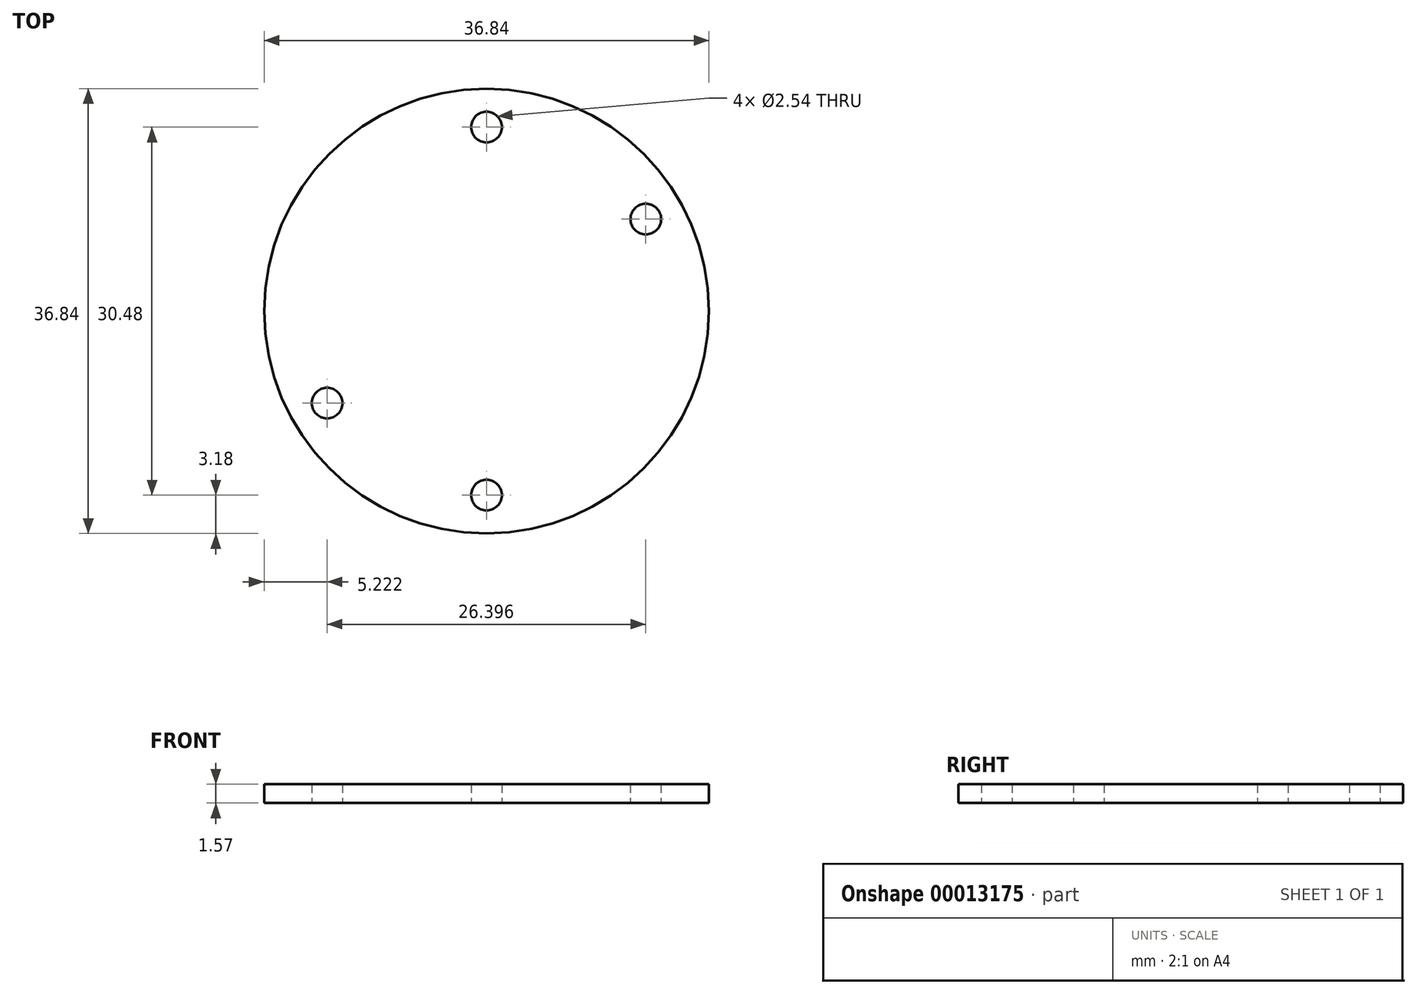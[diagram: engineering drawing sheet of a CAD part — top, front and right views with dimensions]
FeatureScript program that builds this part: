
annotation { "Feature Type Name" : "Feature", "Feature Type Description" : "" }
export const myFeature = defineFeature(function(context is Context, id is Id, definition is map)
    precondition{}
    {
        {
            var Q0;
            Q0=qCreatedBy(makeId("Top.planeOp"),FACE);
            var sketch = newSketch(context, id + "F0", { "sketchPlane" : qUnion([Q0])});
            skCircle(sketch, "E0", {"center": v(0, 0) * mm, "radius": 18.41 * mm});
            skSolve(sketch);
        }
        {
            var Q0;
            Q0=makeQuery(id+"F0.imprint","IMPRINT",FACE,{"disambiguationData":[TD([[makeQuery(id+"F0.imprint","IMPRINT",EDGE,{"derivedFrom":sQuery(id+"F0.wireOp",EDGE,"E0")}),1.0]])]});
            extrude(context, id + "F1", {"entities" : qUnion([Q0]), "depth" : 1.57 * mm});
        }
        {
            var Q0;
            Q0=makeQuery(id+"F1.opExtrude","CAP_FACE",FACE,{"disambiguationData":[OSD([sQuery(id+"F0.wireOp",EDGE,"E0")])],"isStart":true});
            var sketch = newSketch(context, id + "F2", { "sketchPlane" : qUnion([Q0])});
            skLineSegment(sketch, "E1", {"start": v(0, 0) * mm, "end": v(0, -27.69) * mm, "construction": true});
            skLineSegment(sketch, "E2", {"start": v(0, 0) * mm, "end": v(23.53, -13.58) * mm, "construction": true});
            skLineSegment(sketch, "E3", {"start": v(0, 0) * mm, "end": v(-26.4, 15.24) * mm, "construction": true});
            skCircle(sketch, "E4", {"center": v(0, -15.24) * mm, "radius": 1.27 * mm});
            skCircle(sketch, "E5", {"center": v(-13.2, 7.62) * mm, "radius": 1.27 * mm});
            skCircle(sketch, "E6", {"center": v(13.2, -7.62) * mm, "radius": 1.27 * mm});
            skCircle(sketch, "E7", {"center": v(0, 0) * mm, "radius": 15.24 * mm, "construction": true});
            skLineSegment(sketch, "E8", {"start": v(0, 0) * mm, "end": v(0, 19.8) * mm, "construction": true});
            skCircle(sketch, "E9", {"center": v(0, 15.24) * mm, "radius": 1.27 * mm});
            skSolve(sketch);
        }
        {
            var Q0;
            Q0=makeQuery(id+"F2.imprint","IMPRINT",FACE,{"disambiguationData":[TD([[makeQuery(id+"F2.imprint","IMPRINT",EDGE,{"derivedFrom":sQuery(id+"F2.wireOp",EDGE,"E5")}),1.0]])]});
            var Q1;
            Q1=makeQuery(id+"F2.imprint","IMPRINT",FACE,{"disambiguationData":[TD([[makeQuery(id+"F2.imprint","IMPRINT",EDGE,{"derivedFrom":sQuery(id+"F2.wireOp",EDGE,"E6")}),1.0]])]});
            var Q2;
            Q2=makeQuery(id+"F2.imprint","IMPRINT",FACE,{"disambiguationData":[TD([[makeQuery(id+"F2.imprint","IMPRINT",EDGE,{"derivedFrom":sQuery(id+"F2.wireOp",EDGE,"E4")}),1.0]])]});
            var Q3;
            Q3=makeQuery(id+"F2.imprint","IMPRINT",FACE,{"disambiguationData":[TD([[makeQuery(id+"F2.imprint","IMPRINT",EDGE,{"derivedFrom":sQuery(id+"F2.wireOp",EDGE,"E9")}),1.0]])]});
            extrude(context, id + "F3", {"entities" : qUnion([Q0, Q1, Q2, Q3]), "operationType" : NewBodyOperationType.REMOVE, "endBound" : BoundingType.THROUGH_ALL, "oppositeDirection" : true, "depth" : 25.4 * mm});
        }
    });
